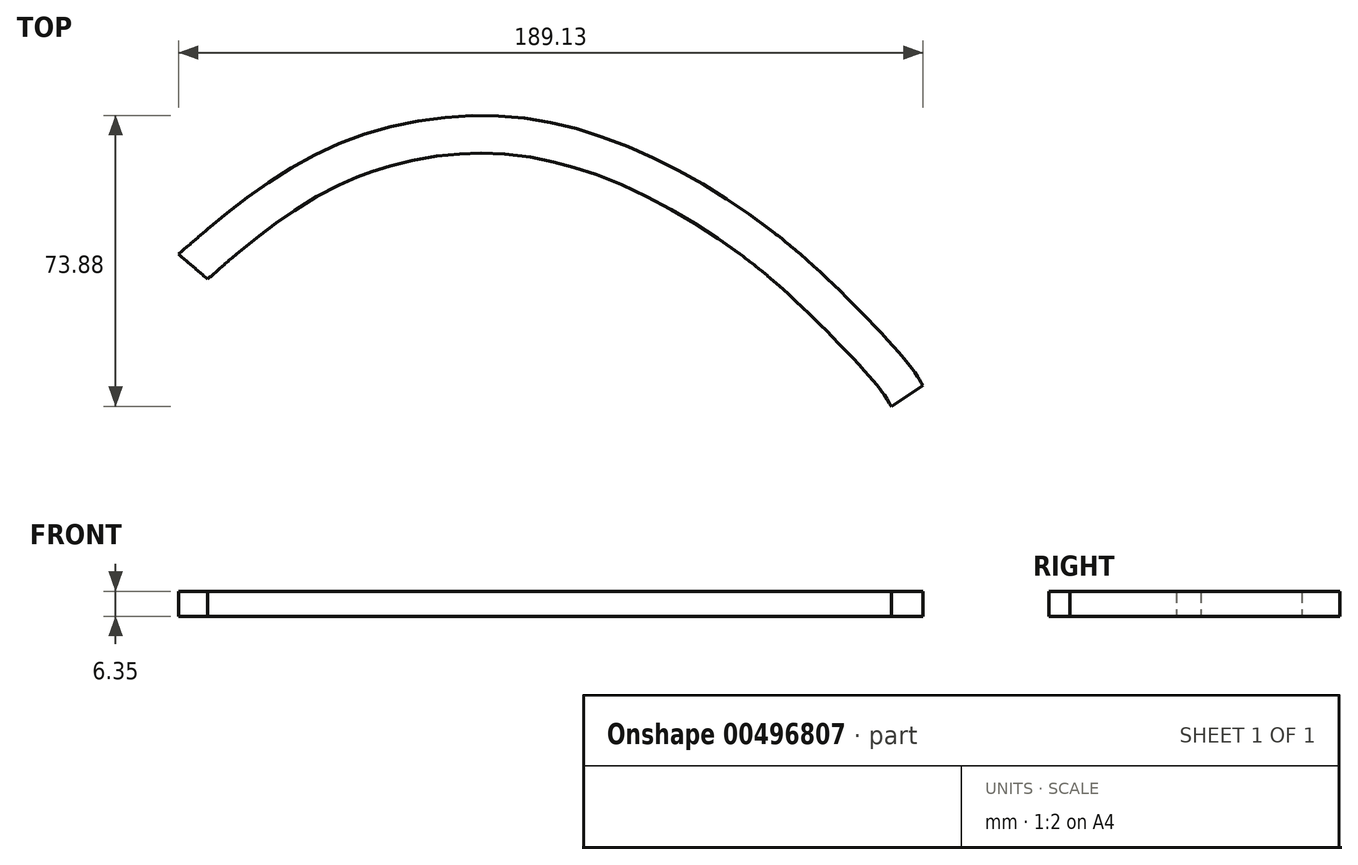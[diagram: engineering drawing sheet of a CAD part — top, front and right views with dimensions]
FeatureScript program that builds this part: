
annotation { "Feature Type Name" : "Feature", "Feature Type Description" : "" }
export const myFeature = defineFeature(function(context is Context, id is Id, definition is map)
    precondition{}
    {
        {
            var Q0;
            Q0=qCreatedBy(makeId("Top.planeOp"),FACE);
            var sketch = newSketch(context, id + "F0", { "sketchPlane" : qUnion([Q0])});
            skFitSpline(sketch, "E0", {"points": [v(0, -39.57) * mm, v(19.12, -23.96) * mm, v(43.28, -10.51) * mm, v(71.59, -4.5) * mm, v(98.2, -6.96) * mm, v(125.64, -17.57) * mm, v(150.11, -33.18) * mm, v(169.77, -50.6) * mm, v(186.21, -68.48) * mm, v(189.13, -72.9) * mm], "startDerivative": vector(163.97, 141.12) * mm, "endDerivative": vector(45.02, -66.87) * mm});
            skLineSegment(sketch, "E1", {"start": v(0, -39.57) * mm, "end": v(190.5, -39.57) * mm, "construction": true});
            skLineSegment(sketch, "E2", {"start": v(181.1, -78.25) * mm, "end": v(189.13, -72.9) * mm});
            skFitSpline(sketch, "E3.0", {"points": [v(3.15, -43.22) * mm, v(6.57, -40.27) * mm, v(11.62, -35.9) * mm, v(17.7, -31.03) * mm, v(21.3, -28.34) * mm, v(24.98, -25.7) * mm, v(29.77, -22.56) * mm, v(35.8, -19.12) * mm, v(41.03, -16.6) * mm, v(45.35, -14.86) * mm, v(49.76, -13.3) * mm, v(55.44, -11.68) * mm, v(62.4, -10.28) * mm, v(68.2, -9.56) * mm, v(72.8, -9.26) * mm, v(77.33, -9.13) * mm, v(82.92, -9.31) * mm, v(89.55, -10.06) * mm, v(95.08, -11.14) * mm, v(99.53, -12.27) * mm, v(104, -13.58) * mm, v(109.61, -15.54) * mm, v(118.55, -19.27) * mm, v(127.3, -23.8) * mm, v(135.62, -28.86) * mm, v(141.59, -32.86) * mm, v(147.23, -37) * mm, v(152.48, -41.19) * mm, v(156.68, -44.83) * mm, v(160.03, -47.9) * mm, v(162.56, -50.3) * mm, v(164.7, -52.37) * mm, v(166.44, -54.1) * mm, v(168.2, -55.85) * mm, v(170.43, -58.1) * mm, v(173.05, -60.82) * mm, v(175.55, -63.48) * mm, v(177.85, -66) * mm, v(179.55, -67.93) * mm, v(180.73, -69.33) * mm, v(181.52, -70.3) * mm, v(182.2, -71.16) * mm, v(182.75, -71.9) * mm, v(183.2, -72.57) * mm, v(183.74, -73.38) * mm, v(184.31, -74.32) * mm, v(184.83, -75.14) * mm, v(185.13, -75.6) * mm], "construction": true});
            skFitSpline(sketch, "E4.MirrorCS", {"points": [v(0, -39.57) * mm, v(19.12, -55.17) * mm, v(43.28, -68.62) * mm, v(71.59, -74.62) * mm, v(98.2, -72.17) * mm, v(125.64, -61.56) * mm, v(150.11, -45.95) * mm, v(169.77, -28.54) * mm, v(186.21, -10.65) * mm, v(189.13, -6.23) * mm], "startDerivative": vector(163.97, -141.12) * mm, "endDerivative": vector(45.02, 66.87) * mm});
            skFitSpline(sketch, "E5.trimOffspring", {"points": [v(6.3, -32.25) * mm, v(9.73, -35.2) * mm, v(14.74, -39.55) * mm, v(20.67, -44.3) * mm, v(24.15, -46.9) * mm, v(27.7, -49.44) * mm, v(32.3, -52.46) * mm, v(38.04, -55.74) * mm, v(42.5, -57.88) * mm, v(45.54, -59.14) * mm, v(47.57, -59.94) * mm, v(50.17, -60.86) * mm, v(53.36, -61.84) * mm, v(57.68, -62.98) * mm, v(63.17, -64.09) * mm, v(68.68, -64.77) * mm, v(73.03, -65.05) * mm, v(77.3, -65.17) * mm, v(82.57, -65) * mm, v(88.82, -64.3) * mm, v(94.03, -63.28) * mm, v(98.25, -62.2) * mm, v(102.5, -60.96) * mm, v(107.88, -59.08) * mm, v(114.33, -56.39) * mm, v(120.7, -53.3) * mm, v(126.96, -49.89) * mm, v(133.02, -46.2) * mm, v(138.82, -42.32) * mm, v(144.3, -38.3) * mm, v(149.39, -34.24) * mm, v(153.47, -30.7) * mm, v(156.74, -27.7) * mm, v(159.22, -25.36) * mm, v(161.32, -23.31) * mm, v(163.04, -21.61) * mm, v(164.78, -19.88) * mm, v(166.98, -17.65) * mm, v(169.56, -14.98) * mm, v(172.01, -12.37) * mm, v(173.89, -10.31) * mm, v(175.25, -8.78) * mm, v(176.18, -7.7) * mm, v(177.03, -6.7) * mm, v(177.76, -5.81) * mm, v(178.26, -5.17) * mm, v(178.6, -4.73) * mm, v(178.89, -4.32) * mm, v(179.2, -3.86) * mm, v(179.65, -3.19) * mm, v(180.07, -2.5) * mm, v(180.61, -1.63) * mm, v(180.94, -1.12) * mm, v(181.12, -0.84) * mm]});
            skFitSpline(sketch, "E6.trimOffspring", {"points": [v(6.3, -46.88) * mm, v(9.73, -43.92) * mm, v(14.74, -39.58) * mm, v(20.67, -34.84) * mm, v(24.15, -32.23) * mm, v(27.7, -29.7) * mm, v(32.3, -26.67) * mm, v(38.04, -23.4) * mm, v(42.5, -21.26) * mm, v(45.54, -20) * mm, v(47.57, -19.2) * mm, v(50.17, -18.27) * mm, v(53.36, -17.3) * mm, v(57.68, -16.15) * mm, v(63.17, -15.04) * mm, v(68.68, -14.37) * mm, v(73.03, -14.08) * mm, v(77.3, -13.96) * mm, v(82.57, -14.13) * mm, v(88.82, -14.84) * mm, v(94.03, -15.85) * mm, v(98.25, -16.93) * mm, v(102.5, -18.17) * mm, v(107.88, -20.05) * mm, v(114.33, -22.74) * mm, v(120.7, -25.82) * mm, v(126.96, -29.24) * mm, v(133.02, -32.93) * mm, v(138.82, -36.81) * mm, v(144.3, -40.83) * mm, v(149.39, -44.9) * mm, v(153.47, -48.44) * mm, v(156.74, -51.43) * mm, v(159.22, -53.77) * mm, v(161.32, -55.82) * mm, v(163.04, -57.52) * mm, v(164.78, -59.25) * mm, v(166.98, -61.48) * mm, v(169.56, -64.15) * mm, v(172.01, -66.76) * mm, v(173.89, -68.82) * mm, v(175.25, -70.35) * mm, v(176.18, -71.43) * mm, v(177.03, -72.42) * mm, v(177.76, -73.32) * mm, v(178.26, -73.96) * mm, v(178.6, -74.4) * mm, v(178.89, -74.8) * mm, v(179.2, -75.27) * mm, v(179.65, -75.95) * mm, v(180.07, -76.63) * mm, v(180.61, -77.5) * mm, v(180.94, -78.01) * mm, v(181.12, -78.29) * mm]});
            skFitSpline(sketch, "E7.trimOffspring", {"points": [v(6.28, -32.27) * mm, v(9.72, -35.22) * mm, v(14.72, -39.56) * mm, v(20.66, -44.31) * mm, v(24.14, -46.92) * mm, v(27.69, -49.46) * mm, v(32.29, -52.48) * mm, v(38.03, -55.76) * mm, v(42.5, -57.9) * mm, v(45.53, -59.16) * mm, v(47.57, -59.96) * mm, v(50.16, -60.88) * mm, v(53.35, -61.86) * mm, v(57.67, -63) * mm, v(63.17, -64.1) * mm, v(68.68, -64.79) * mm, v(73.02, -65.07) * mm, v(77.3, -65.2) * mm, v(82.57, -65.02) * mm, v(88.82, -64.31) * mm, v(94.03, -63.3) * mm, v(98.25, -62.23) * mm, v(102.51, -60.98) * mm, v(107.88, -59.1) * mm, v(114.33, -56.4) * mm, v(120.72, -53.33) * mm, v(126.97, -49.9) * mm, v(133.03, -46.22) * mm, v(138.83, -42.34) * mm, v(144.31, -38.32) * mm, v(149.4, -34.25) * mm, v(153.49, -30.7) * mm, v(156.76, -27.71) * mm, v(159.24, -25.37) * mm, v(161.34, -23.33) * mm, v(163.06, -21.63) * mm, v(164.8, -19.9) * mm, v(167, -17.67) * mm, v(169.57, -15) * mm, v(172.03, -12.38) * mm, v(173.9, -10.33) * mm, v(175.26, -8.8) * mm, v(176.2, -7.72) * mm, v(177.04, -6.72) * mm, v(177.78, -5.83) * mm, v(178.28, -5.18) * mm, v(178.61, -4.74) * mm, v(178.9, -4.34) * mm, v(179.23, -3.88) * mm, v(179.67, -3.2) * mm, v(180.1, -2.5) * mm, v(180.63, -1.64) * mm, v(180.96, -1.13) * mm, v(181.14, -0.86) * mm]});
            skFitSpline(sketch, "E8.trimOffspring", {"points": [v(6.28, -46.86) * mm, v(9.72, -43.9) * mm, v(14.72, -39.57) * mm, v(20.66, -34.82) * mm, v(24.14, -32.21) * mm, v(27.69, -29.67) * mm, v(32.29, -26.66) * mm, v(38.03, -23.37) * mm, v(42.5, -21.24) * mm, v(45.53, -19.97) * mm, v(47.57, -19.17) * mm, v(50.16, -18.25) * mm, v(53.35, -17.27) * mm, v(57.67, -16.13) * mm, v(63.17, -15.02) * mm, v(68.68, -14.34) * mm, v(73.02, -14.06) * mm, v(77.3, -13.94) * mm, v(82.57, -14.1) * mm, v(88.82, -14.82) * mm, v(94.03, -15.83) * mm, v(98.25, -16.9) * mm, v(102.51, -18.15) * mm, v(107.88, -20.03) * mm, v(114.33, -22.72) * mm, v(120.72, -25.8) * mm, v(126.97, -29.22) * mm, v(133.03, -32.9) * mm, v(138.83, -36.8) * mm, v(144.31, -40.8) * mm, v(149.4, -44.88) * mm, v(153.49, -48.42) * mm, v(156.76, -51.42) * mm, v(159.24, -53.76) * mm, v(161.34, -55.8) * mm, v(163.06, -57.5) * mm, v(164.8, -59.24) * mm, v(167, -61.46) * mm, v(169.57, -64.14) * mm, v(172.03, -66.75) * mm, v(173.9, -68.8) * mm, v(175.26, -70.33) * mm, v(176.2, -71.41) * mm, v(177.04, -72.4) * mm, v(177.78, -73.3) * mm, v(178.28, -73.95) * mm, v(178.61, -74.39) * mm, v(178.9, -74.8) * mm, v(179.23, -75.25) * mm, v(179.67, -75.93) * mm, v(180.1, -76.62) * mm, v(180.63, -77.5) * mm, v(180.96, -78) * mm, v(181.14, -78.27) * mm]});
            skFitSpline(sketch, "E9.trimOffspring", {"points": [v(3.15, -35.9) * mm, v(6.57, -38.86) * mm, v(11.62, -43.23) * mm, v(17.7, -48.1) * mm, v(21.3, -50.8) * mm, v(24.98, -53.43) * mm, v(29.77, -56.57) * mm, v(35.8, -60.01) * mm, v(41.03, -62.52) * mm, v(45.35, -64.27) * mm, v(49.76, -65.83) * mm, v(55.44, -67.45) * mm, v(62.4, -68.85) * mm, v(68.2, -69.57) * mm, v(72.8, -69.87) * mm, v(77.33, -70) * mm, v(82.92, -69.82) * mm, v(89.55, -69.07) * mm, v(95.08, -68) * mm, v(99.53, -66.86) * mm, v(104, -65.55) * mm, v(109.61, -63.6) * mm, v(118.55, -59.86) * mm, v(127.3, -55.34) * mm, v(135.62, -50.27) * mm, v(141.59, -46.27) * mm, v(147.23, -42.14) * mm, v(152.48, -37.94) * mm, v(156.68, -34.3) * mm, v(160.03, -31.23) * mm, v(162.56, -28.84) * mm, v(164.7, -26.76) * mm, v(166.44, -25.04) * mm, v(168.2, -23.28) * mm, v(170.43, -21.02) * mm, v(173.05, -18.3) * mm, v(175.55, -15.65) * mm, v(177.85, -13.13) * mm, v(179.55, -11.2) * mm, v(180.73, -9.8) * mm, v(181.52, -8.83) * mm, v(182.2, -7.97) * mm, v(182.75, -7.23) * mm, v(183.2, -6.56) * mm, v(183.74, -5.75) * mm, v(184.31, -4.81) * mm, v(184.83, -3.99) * mm, v(185.13, -3.54) * mm], "construction": true});
            skLineSegment(sketch, "E10", {"start": v(181.1, -0.88) * mm, "end": v(189.13, -6.23) * mm});
            skFitSpline(sketch, "E11.0", {"points": [v(3.15, -35.9) * mm, v(6.58, -38.86) * mm, v(11.62, -43.23) * mm, v(17.7, -48.1) * mm, v(21.3, -50.8) * mm, v(24.98, -53.42) * mm, v(29.77, -56.57) * mm, v(35.8, -60.01) * mm, v(41.03, -62.52) * mm, v(45.35, -64.27) * mm, v(49.76, -65.83) * mm, v(55.44, -67.45) * mm, v(62.4, -68.85) * mm, v(68.2, -69.57) * mm, v(72.8, -69.87) * mm, v(77.33, -70) * mm, v(82.92, -69.82) * mm, v(89.55, -69.07) * mm, v(95.08, -68) * mm, v(99.53, -66.86) * mm, v(104, -65.55) * mm, v(109.61, -63.6) * mm, v(116.31, -60.8) * mm, v(122.92, -57.6) * mm, v(129.37, -54.07) * mm, v(135.62, -50.27) * mm, v(141.59, -46.27) * mm, v(147.23, -42.14) * mm, v(152.48, -37.94) * mm, v(156.68, -34.3) * mm, v(160.03, -31.23) * mm, v(162.56, -28.84) * mm, v(164.7, -26.76) * mm, v(166.44, -25.04) * mm, v(168.2, -23.28) * mm, v(170.43, -21.02) * mm, v(173.05, -18.3) * mm, v(175.55, -15.65) * mm, v(177.85, -13.13) * mm, v(179.55, -11.2) * mm, v(180.73, -9.8) * mm, v(181.52, -8.83) * mm, v(182.2, -7.97) * mm, v(182.75, -7.23) * mm, v(183.2, -6.57) * mm, v(183.6, -5.96) * mm, v(183.9, -5.47) * mm, v(184.15, -5.1) * mm, v(184.39, -4.7) * mm, v(184.7, -4.2) * mm, v(184.98, -3.76) * mm, v(185.13, -3.54) * mm], "construction": true});
            skSolve(sketch);
        }
        {
            var Q0;
            Q0=makeQuery(id+"F0.imprint","IMPRINT",FACE,{"disambiguationData":[TD([[makeQuery(id+"F0.imprint","IMPRINT",EDGE,{"derivedFrom":sQuery(id+"F0.wireOp",EDGE,"E0")}),-1.0]])]});
            extrude(context, id + "F1", {"entities" : qUnion([Q0]), "depth" : 6.35 * mm});
        }
    });
